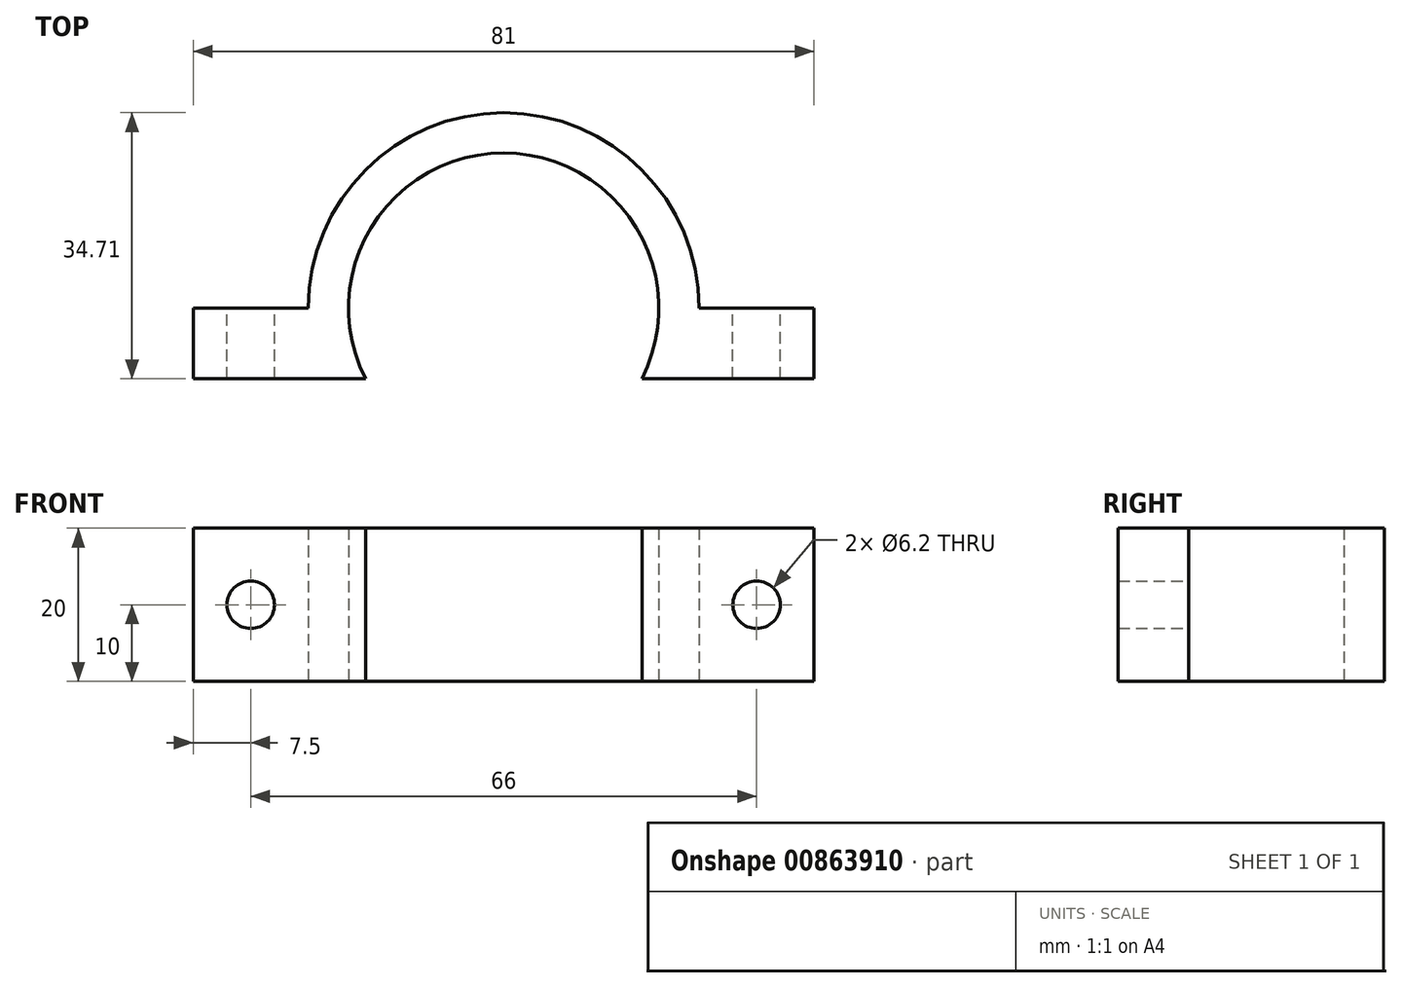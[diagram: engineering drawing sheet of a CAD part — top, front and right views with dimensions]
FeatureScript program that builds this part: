
annotation { "Feature Type Name" : "Feature", "Feature Type Description" : "" }
export const myFeature = defineFeature(function(context is Context, id is Id, definition is map)
    precondition{}
    {
        {
            var Q0;
            Q0=qCreatedBy(makeId("Top.planeOp"),FACE);
            var sketch = newSketch(context, id + "F0", { "sketchPlane" : qUnion([Q0])});
            skCircle(sketch, "E0", {"center": v(0, 0) * mm, "radius": 20.25 * mm});
            skCircle(sketch, "E1", {"center": v(0, 0) * mm, "radius": 25.5 * mm});
            skLineSegment(sketch, "E2.bottom", {"start": v(-40.5, 0) * mm, "end": v(40.5, 0) * mm});
            skLineSegment(sketch, "E2.top", {"start": v(-40.5, -9.2) * mm, "end": v(40.5, -9.2) * mm});
            skLineSegment(sketch, "E2.left", {"start": v(-40.5, 0) * mm, "end": v(-40.5, -9.2) * mm});
            skLineSegment(sketch, "E2.right", {"start": v(40.5, 0) * mm, "end": v(40.5, -9.2) * mm});
            skSolve(sketch);
        }
        {
            var Q0;
            {var subQ5=sQuery(id+"F0.wireOp",EDGE,"E2.left");Q0=makeQuery(id+"F0.imprint","IMPRINT",FACE,{"disambiguationData":[TD([[makeQuery(id+"F0.imprint","IMPRINT",EDGE,{"derivedFrom":subQ5}),1.0]])]});}
            var Q1;
            {var subQ5=sQuery(id+"F0.wireOp",EDGE,"E2.right");Q1=makeQuery(id+"F0.imprint","IMPRINT",FACE,{"disambiguationData":[TD([[makeQuery(id+"F0.imprint","IMPRINT",EDGE,{"derivedFrom":subQ5}),-1.0]])]});}
            var Q2;
            {var subQ0=sQuery(id+"F0.wireOp",EDGE,"E2.bottom");var subQ1=sQuery(id+"F0.wireOp",EDGE,"E0");var subQ2=makeQuery(id+"F0.imprint","INTERSECT",VERTEX,{"disambiguationData":[OD(0.0)],"derivedFrom":[subQ1,subQ0]});Q2=makeQuery(id+"F0.imprint","IMPRINT",FACE,{"disambiguationData":[TD([[makeQuery(id+"F0.imprint","IMPRINT",EDGE,{"disambiguationData":[TD([[subQ2,1.0]])],"derivedFrom":subQ1}),-1.0]])]});}
            var Q3;
            {var subQ0=sQuery(id+"F0.wireOp",EDGE,"E2.bottom");var subQ1=sQuery(id+"F0.wireOp",EDGE,"E0");var subQ2=makeQuery(id+"F0.imprint","INTERSECT",VERTEX,{"disambiguationData":[OD(0.0)],"derivedFrom":[subQ1,subQ0]});Q3=makeQuery(id+"F0.imprint","IMPRINT",FACE,{"disambiguationData":[TD([[makeQuery(id+"F0.imprint","IMPRINT",EDGE,{"disambiguationData":[TD([[subQ2,-1.0]])],"derivedFrom":subQ1}),-1.0]])]});}
            var Q4;
            {var subQ0=sQuery(id+"F0.wireOp",EDGE,"E2.bottom");var subQ1=sQuery(id+"F0.wireOp",EDGE,"E0");var subQ2=makeQuery(id+"F0.imprint","INTERSECT",VERTEX,{"disambiguationData":[OD(1.0)],"derivedFrom":[subQ1,subQ0]});Q4=makeQuery(id+"F0.imprint","IMPRINT",FACE,{"disambiguationData":[TD([[makeQuery(id+"F0.imprint","IMPRINT",EDGE,{"disambiguationData":[TD([[subQ2,1.0]])],"derivedFrom":subQ1}),-1.0]])]});}
            extrude(context, id + "F1", {"entities" : qUnion([Q0, Q1, Q2, Q3, Q4]), "depth" : 20 * mm, "offsetDistance" : 25 * mm});
        }
        {
            var Q0;
            {var subQ0=sQuery(id+"F0.wireOp",EDGE,"E2.bottom");Q0=makeQuery(id+"F1.opExtrude","SWEPT_FACE",FACE,{"disambiguationData":[OSD([subQ0]),TDD([makeQuery(id+"F0.imprint","IMPRINT",EDGE,{"disambiguationData":[TD([[makeQuery(id+"F0.imprint","INTERSECT",VERTEX,{"derivedFrom":[subQ0,sQuery(id+"F0.wireOp",EDGE,"E2.left")]}),-1.0]])],"derivedFrom":subQ0})])]});}
            var sketch = newSketch(context, id + "F2", { "sketchPlane" : qUnion([Q0])});
            skLineSegment(sketch, "E3", {"start": v(25.5, 20) * mm, "end": v(40.5, 20) * mm});
            skCircle(sketch, "E4", {"center": v(33, 10) * mm, "radius": 3.1 * mm});
            skSolve(sketch);
        }
        {
            var Q0;
            {var subQ0=sQuery(id+"F0.wireOp",EDGE,"E2.bottom");Q0=makeQuery(id+"F1.opExtrude","SWEPT_FACE",FACE,{"disambiguationData":[OSD([subQ0]),TDD([makeQuery(id+"F0.imprint","IMPRINT",EDGE,{"disambiguationData":[TD([[makeQuery(id+"F0.imprint","INTERSECT",VERTEX,{"derivedFrom":[subQ0,sQuery(id+"F0.wireOp",EDGE,"E2.right")]}),1.0]])],"derivedFrom":subQ0})])]});}
            var sketch = newSketch(context, id + "F3", { "sketchPlane" : qUnion([Q0])});
            skLineSegment(sketch, "E5", {"start": v(-40.5, 20) * mm, "end": v(-40.5, 0) * mm});
            skCircle(sketch, "E6", {"center": v(-33, 10) * mm, "radius": 3.1 * mm});
            skSolve(sketch);
        }
        {
            var Q0;
            Q0=makeQuery(id+"F2.imprint","IMPRINT",FACE,{"disambiguationData":[TD([[makeQuery(id+"F2.imprint","IMPRINT",EDGE,{"derivedFrom":sQuery(id+"F2.wireOp",EDGE,"E4")}),1.0]])]});
            var Q1;
            Q1=makeQuery(id+"F3.imprint","IMPRINT",FACE,{"disambiguationData":[TD([[makeQuery(id+"F3.imprint","IMPRINT",EDGE,{"derivedFrom":sQuery(id+"F3.wireOp",EDGE,"E6")}),1.0]])]});
            extrude(context, id + "F4", {"entities" : qUnion([Q0, Q1]), "operationType" : NewBodyOperationType.REMOVE, "oppositeDirection" : true, "depth" : 25 * mm, "offsetDistance" : 25 * mm});
        }
    });
